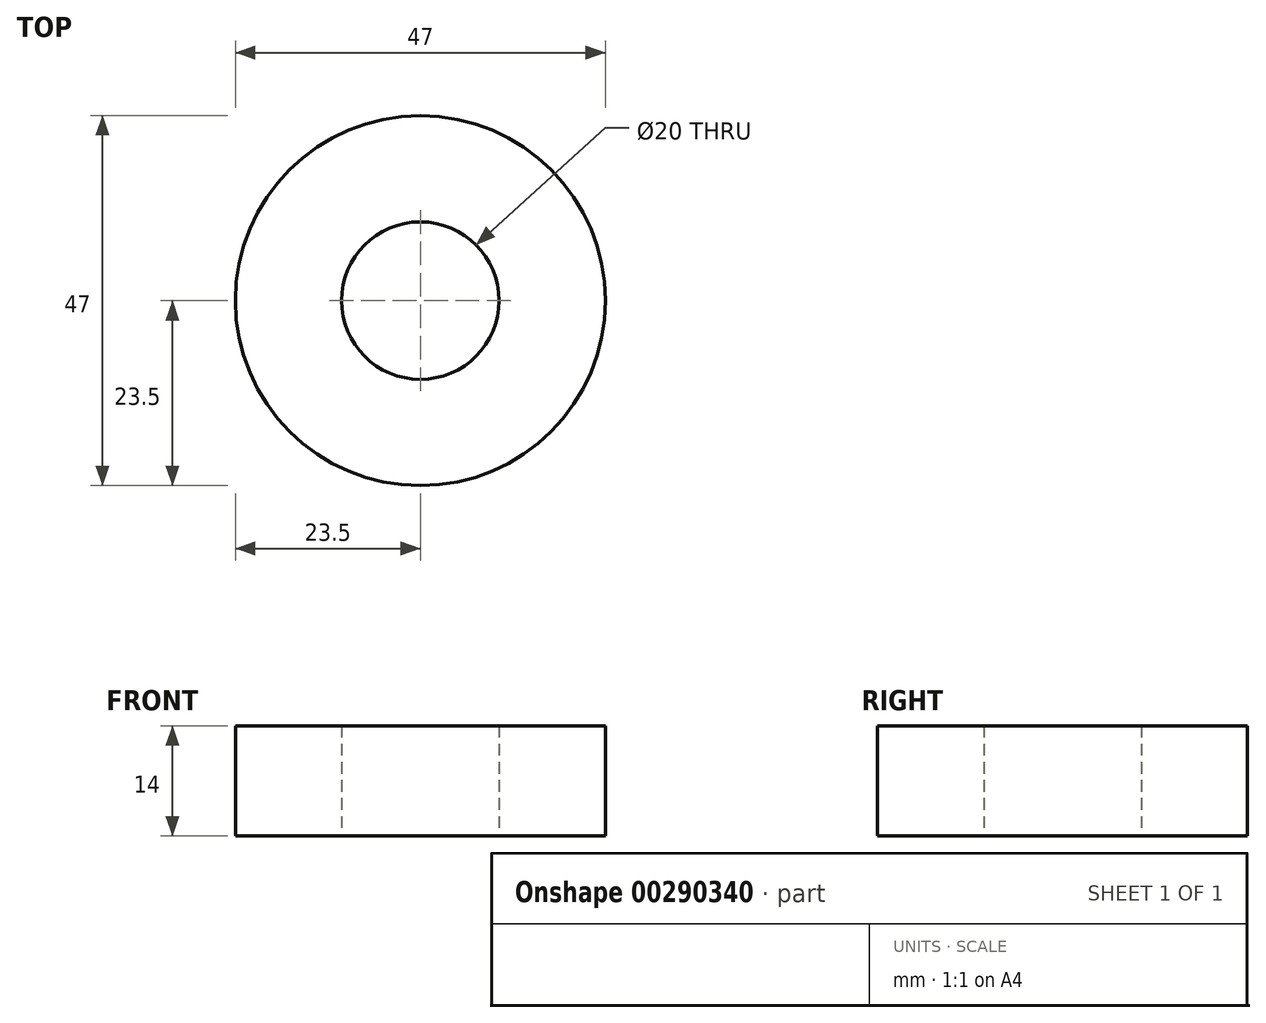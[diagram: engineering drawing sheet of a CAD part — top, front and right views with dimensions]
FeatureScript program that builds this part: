
annotation { "Feature Type Name" : "Feature", "Feature Type Description" : "" }
export const myFeature = defineFeature(function(context is Context, id is Id, definition is map)
    precondition{}
    {
        {
            var Q0;
            Q0=qCreatedBy(makeId("Top.planeOp"),FACE);
            var sketch = newSketch(context, id + "F0", { "sketchPlane" : qUnion([Q0])});
            skCircle(sketch, "E0", {"center": v(0, 0) * mm, "radius": 10 * mm});
            skCircle(sketch, "E1", {"center": v(0, 0) * mm, "radius": 23.5 * mm});
            skSolve(sketch);
        }
        {
            var Q0;
            Q0 = qSketchRegion(id + "F0", true);
            extrude(context, id + "F1", {"entities" : qUnion([Q0]), "depth" : 14 * mm});
        }
    });
